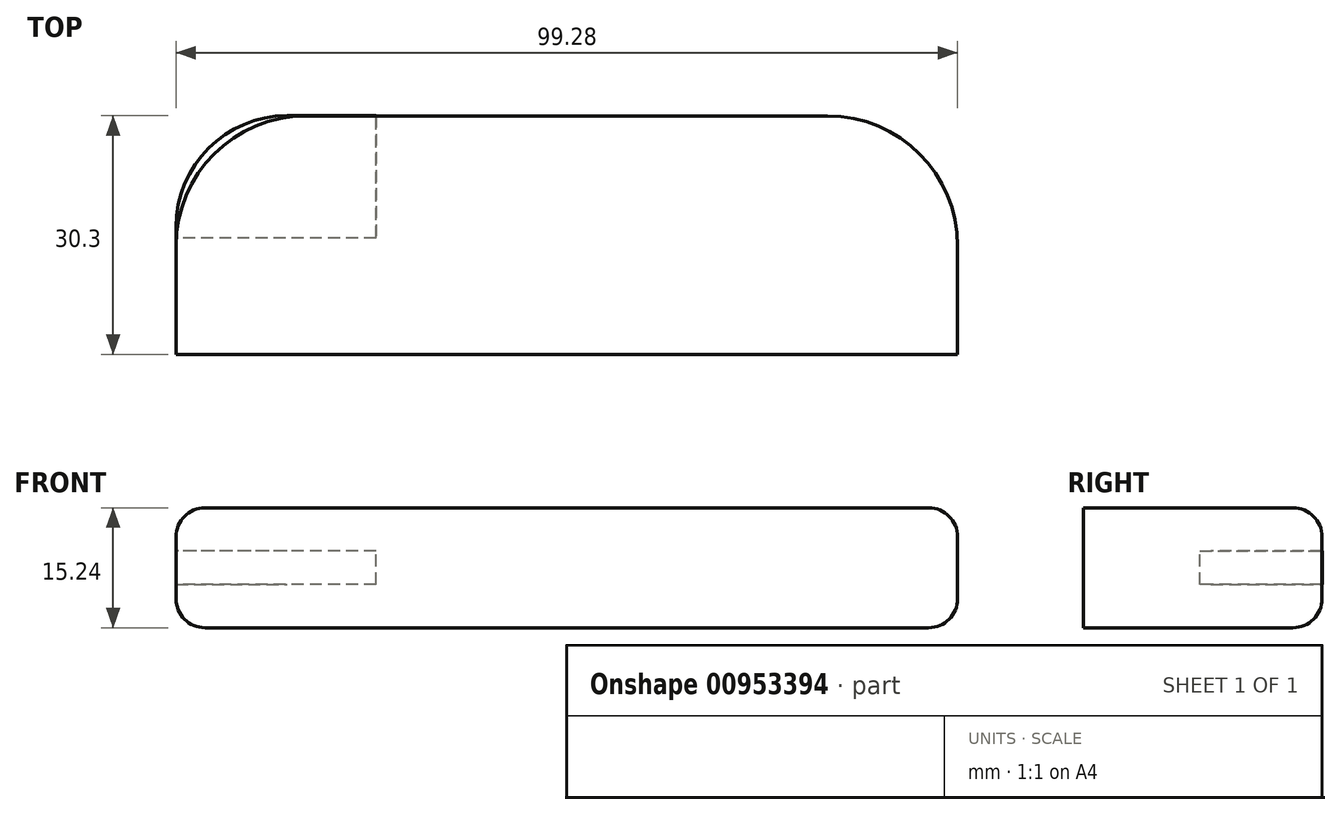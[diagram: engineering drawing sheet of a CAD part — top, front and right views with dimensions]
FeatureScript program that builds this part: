
annotation { "Feature Type Name" : "Feature", "Feature Type Description" : "" }
export const myFeature = defineFeature(function(context is Context, id is Id, definition is map)
    precondition{}
    {
        {
            var Q0;
            Q0=qCreatedBy(makeId("Top.planeOp"),FACE);
            var sketch = newSketch(context, id + "F0", { "sketchPlane" : qUnion([Q0])});
            skLineSegment(sketch, "E0.bottom", {"start": v(-29.95, -18.44) * mm, "end": v(36.3, -18.44) * mm});
            skLineSegment(sketch, "E0.top", {"start": v(-46.46, -48.71) * mm, "end": v(52.82, -48.71) * mm});
            skLineSegment(sketch, "E0.left", {"start": v(-46.46, -34.95) * mm, "end": v(-46.46, -48.71) * mm});
            skLineSegment(sketch, "E0.right", {"start": v(52.82, -34.95) * mm, "end": v(52.82, -48.71) * mm});
            skPoint(sketch, "E1.visualSharp", {"position": v(52.82, -18.44) * mm});
            skArc(sketch, "E1.filletArc", {"start": v(52.82, -34.95) * mm, "mid": v(47.98, -23.27) * mm, "end": v(36.3, -18.44) * mm});
            skPoint(sketch, "E2.visualSharp", {"position": v(-46.46, -18.44) * mm});
            skArc(sketch, "E2.filletArc", {"start": v(-29.95, -18.44) * mm, "mid": v(-41.62, -23.27) * mm, "end": v(-46.46, -34.95) * mm});
            skSolve(sketch);
        }
        {
            var Q0;
            Q0=qSketchRegion(id+"F0",true);
            extrude(context, id + "F1", {"entities" : qUnion([Q0]), "depth" : 15.24 * mm, "offsetDistance" : 25.4 * mm});
        }
        {
            var Q0;
            Q0=makeQuery(id+"F1.opExtrude","CAP_EDGE",EDGE,{"disambiguationData":[OSD([sQuery(id+"F0.wireOp",EDGE,"E0.bottom")])],"isStart":false});
            var Q1;
            Q1=makeQuery(id+"F1.opExtrude","CAP_EDGE",EDGE,{"disambiguationData":[OSD([sQuery(id+"F0.wireOp",EDGE,"E0.bottom")])],"isStart":true});
            fillet(context, id + "F2", {"entities" : qUnion([Q0, Q1]), "radius" : 3.68 * mm, "tangentPropagation" : true, "allowEdgeOverflow" : false});
        }
        {
            var Q0;
            Q0=makeQuery(id+"F1.opExtrude","SWEPT_FACE",FACE,{"disambiguationData":[OSD([sQuery(id+"F0.wireOp",EDGE,"E0.left")])]});
            var sketch = newSketch(context, id + "F3", { "sketchPlane" : qUnion([Q0])});
            skLineSegment(sketch, "E3", {"start": v(33.93, 9.75) * mm, "end": v(18.4, 9.75) * mm});
            skLineSegment(sketch, "E4", {"start": v(18.4, 9.75) * mm, "end": v(18.4, 5.52) * mm});
            skLineSegment(sketch, "E5", {"start": v(18.4, 5.52) * mm, "end": v(33.93, 5.52) * mm});
            skLineSegment(sketch, "E6", {"start": v(33.93, 5.52) * mm, "end": v(33.93, 9.75) * mm});
            skSolve(sketch);
        }
        {
            var Q0;
            Q0=qSketchRegion(id+"F3",true);
            extrude(context, id + "F4", {"entities" : qUnion([Q0]), "oppositeDirection" : true, "depth" : 25.4 * mm, "offsetDistance" : 25.4 * mm});
        }
        {
            var Q0;
            Q0=makeQuery(id+"F4.opExtrude","CAP_EDGE",EDGE,{"disambiguationData":[OSD([sQuery(id+"F3.wireOp",EDGE,"E4")])],"isStart":true});
            fillet(context, id + "F5", {"entities" : qUnion([Q0]), "radius" : 14.1 * mm, "tangentPropagation" : true, "allowEdgeOverflow" : false});
        }
    });
